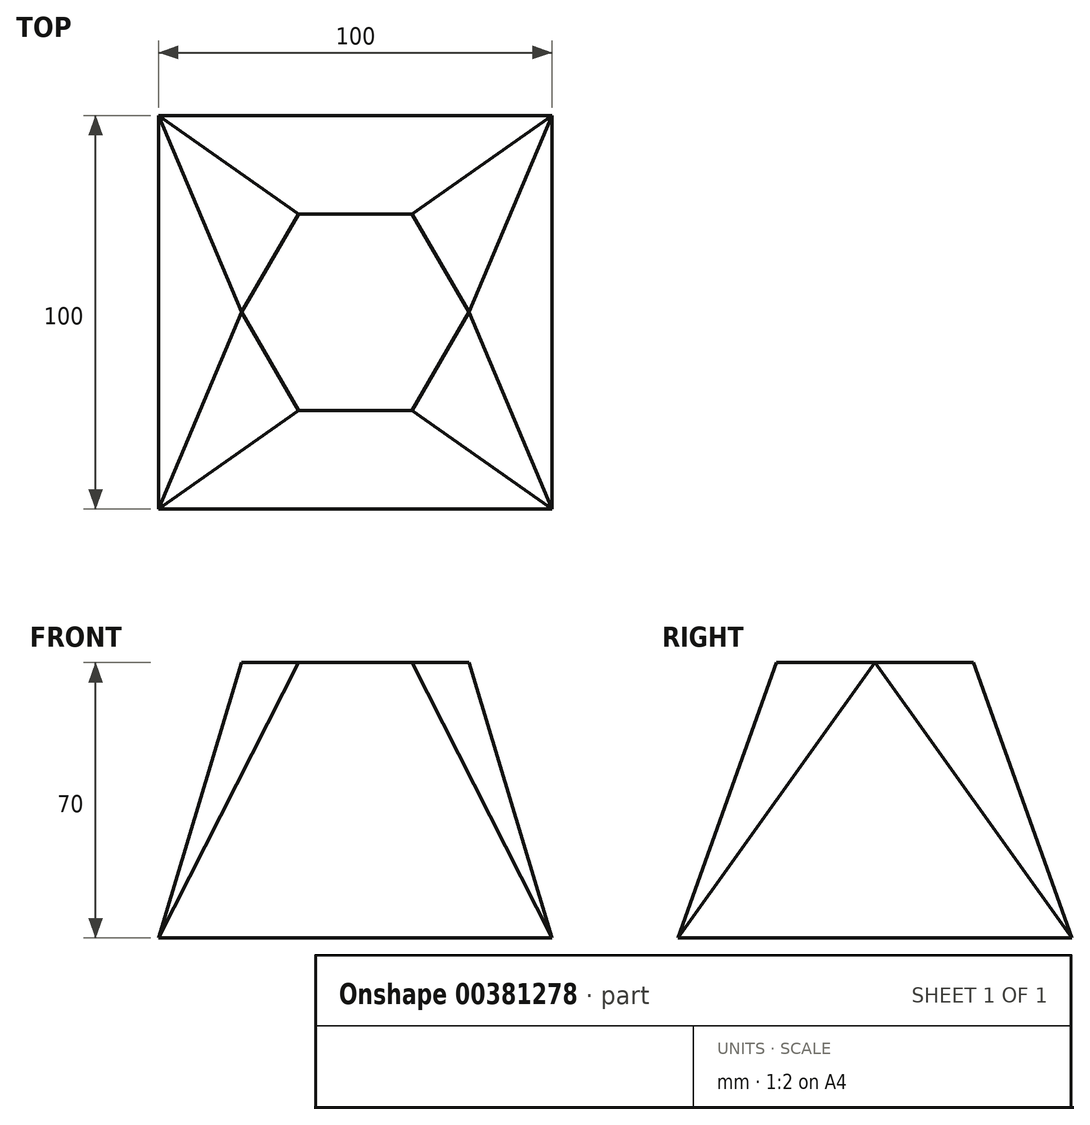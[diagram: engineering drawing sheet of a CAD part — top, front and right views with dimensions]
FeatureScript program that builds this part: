
annotation { "Feature Type Name" : "Feature", "Feature Type Description" : "" }
export const myFeature = defineFeature(function(context is Context, id is Id, definition is map)
    precondition{}
    {
        {
            var Q0;
            Q0=qCreatedBy(makeId("Top.planeOp"),FACE);
            cPlane(context, id + "F0", {"entities" : qUnion([Q0]), "cplaneType" : CPlaneType.OFFSET, "offset" : 70 * mm, "width" : 150 * mm, "height" : 150 * mm});
        }
        {
            var Q0;
            Q0=qCreatedBy(makeId("Top.planeOp"),FACE);
            var sketch = newSketch(context, id + "F1", { "sketchPlane" : qUnion([Q0])});
            skLineSegment(sketch, "E0.bottom", {"start": v(50, 50) * mm, "end": v(-50, 50) * mm});
            skLineSegment(sketch, "E0.top", {"start": v(50, -50) * mm, "end": v(-50, -50) * mm});
            skLineSegment(sketch, "E0.left", {"start": v(50, 50) * mm, "end": v(50, -50) * mm});
            skLineSegment(sketch, "E0.right", {"start": v(-50, 50) * mm, "end": v(-50, -50) * mm});
            skPoint(sketch, "E0.middle", {"position": v(0, 0) * mm});
            skSolve(sketch);
        }
        {
            var Q0;
            Q0=qCreatedBy(id+"F0.planeOp",FACE);
            var sketch = newSketch(context, id + "F2", { "sketchPlane" : qUnion([Q0])});
            skCircle(sketch, "E1.cCircle", {"center": v(0, 0) * mm, "radius": 25 * mm, "construction": true});
            skLineSegment(sketch, "E1.0", {"start": v(-14.43, 25) * mm, "end": v(14.43, 25) * mm});
            skLineSegment(sketch, "E1.1", {"start": v(14.43, 25) * mm, "end": v(28.87, 0) * mm});
            skLineSegment(sketch, "E1.2", {"start": v(28.87, 0) * mm, "end": v(14.43, -25) * mm});
            skLineSegment(sketch, "E1.3", {"start": v(14.43, -25) * mm, "end": v(-14.43, -25) * mm});
            skLineSegment(sketch, "E1.4", {"start": v(-14.43, -25) * mm, "end": v(-28.87, 0) * mm});
            skLineSegment(sketch, "E1.5", {"start": v(-28.87, 0) * mm, "end": v(-14.43, 25) * mm});
            skPoint(sketch, "E1.0.midPoint", {"position": v(0, 25) * mm});
            skSolve(sketch);
        }
        {
            var Q0;
            Q0=qCreatedBy(id+"F0.planeOp",FACE);
            var sketch = newSketch(context, id + "F3", { "sketchPlane" : qUnion([Q0])});
            skLineSegment(sketch, "E2.bottom", {"start": v(-28.87, 25) * mm, "end": v(28.87, 25) * mm});
            skLineSegment(sketch, "E2.top", {"start": v(-28.87, -25) * mm, "end": v(28.87, -25) * mm});
            skLineSegment(sketch, "E2.left", {"start": v(-28.87, 25) * mm, "end": v(-28.87, -25) * mm});
            skLineSegment(sketch, "E2.right", {"start": v(28.87, 25) * mm, "end": v(28.87, -25) * mm});
            skPoint(sketch, "E2.middle", {"position": v(0, 0) * mm});
            skSolve(sketch);
        }
        {
            var Q0;
            Q0=makeQuery(id+"F3.imprint","IMPRINT",FACE,{"disambiguationData":[TD([[makeQuery(id+"F3.imprint","IMPRINT",EDGE,{"derivedFrom":sQuery(id+"F3.wireOp",EDGE,"E2.bottom")}),-1.0]])]});
            var Q1;
            Q1=makeQuery(id+"F1.imprint","IMPRINT",FACE,{"disambiguationData":[TD([[makeQuery(id+"F1.imprint","IMPRINT",EDGE,{"derivedFrom":sQuery(id+"F1.wireOp",EDGE,"E0.bottom")}),1.0]])]});
            loft(context, id + "F4", {"sheetProfilesArray" : [{ "sheetProfileEntities" : qUnion([Q0]) }, { "sheetProfileEntities" : qUnion([Q1]) }]});
        }
        {
            var Q0;
            Q0=qCreatedBy(id+"F0.planeOp",FACE);
            var sketch = newSketch(context, id + "F5", { "sketchPlane" : qUnion([Q0])});
            skLineSegment(sketch, "E3", {"start": v(14.43, 25) * mm, "end": v(28.87, 0) * mm});
            skLineSegment(sketch, "E4", {"start": v(28.87, 0) * mm, "end": v(28.87, 25) * mm});
            skLineSegment(sketch, "E5", {"start": v(28.87, 25) * mm, "end": v(14.43, 25) * mm});
            skSolve(sketch);
        }
        {
            var Q1;
            Q1=makeQuery(id+"F5.imprint","IMPRINT",FACE,{"disambiguationData":[TD([[makeQuery(id+"F5.imprint","IMPRINT",EDGE,{"derivedFrom":sQuery(id+"F5.wireOp",EDGE,"E3")}),1.0]])]});
            var Q2;
            Q2=makeQuery(id+"F4.opLoft","MID_CAP_VERTEX",VERTEX,{"disambiguationData":[OSD([sQuery(id+"F1.wireOp",EDGE,"E0.bottom"),sQuery(id+"F1.wireOp",EDGE,"E0.left")])],"capPos":1.0});
            loft(context, id + "F6", {"sheetProfilesArray" : [{ "sheetProfileEntities" : qUnion([Q1]) }, { "sheetProfileEntities" : qUnion([Q2]) }]});
        }
        {
            var Q0;
            Q0=makeQuery(id+"F6.opLoft","SWEPT_BODY",BODY,{"disambiguationData":[OSD([sQuery(id+"F1.wireOp",EDGE,"E0.bottom"),sQuery(id+"F1.wireOp",EDGE,"E0.left"),makeQuery(id+"F5.imprint","IMPRINT",FACE,{"disambiguationData":[TD([[makeQuery(id+"F5.imprint","IMPRINT",EDGE,{"derivedFrom":sQuery(id+"F5.wireOp",EDGE,"E3")}),1.0]])]})])]});
            var Q1;
            Q1=qCreatedBy(makeId("Right.planeOp"),FACE);
            mirror(context, id + "F7", {"entities" : qUnion([Q0]), "mirrorPlane" : qUnion([Q1])});
        }
        {
            var Q0;
            Q0=makeQuery(id+"F6.opLoft","SWEPT_BODY",BODY,{"disambiguationData":[OSD([sQuery(id+"F1.wireOp",EDGE,"E0.bottom"),sQuery(id+"F1.wireOp",EDGE,"E0.left"),makeQuery(id+"F5.imprint","IMPRINT",FACE,{"disambiguationData":[TD([[makeQuery(id+"F5.imprint","IMPRINT",EDGE,{"derivedFrom":sQuery(id+"F5.wireOp",EDGE,"E3")}),1.0]])]})])]});
            var Q1;
            Q1=makeQuery(id+"F7.opPattern","COPY",BODY,{"derivedFrom":makeQuery(id+"F6.opLoft","SWEPT_BODY",BODY,{"disambiguationData":[OSD([sQuery(id+"F1.wireOp",EDGE,"E0.bottom"),sQuery(id+"F1.wireOp",EDGE,"E0.left"),makeQuery(id+"F5.imprint","IMPRINT",FACE,{"disambiguationData":[TD([[makeQuery(id+"F5.imprint","IMPRINT",EDGE,{"derivedFrom":sQuery(id+"F5.wireOp",EDGE,"E3")}),1.0]])]})])]}),"instanceName":"1"});
            var Q2;
            Q2=qCreatedBy(makeId("Front.planeOp"),FACE);
            mirror(context, id + "F8", {"entities" : qUnion([Q0, Q1]), "mirrorPlane" : qUnion([Q2])});
        }
        {
            var Q0;
            Q0=makeQuery(id+"F8.opPattern","COPY",BODY,{"derivedFrom":makeQuery(id+"F7.opPattern","COPY",BODY,{"derivedFrom":makeQuery(id+"F6.opLoft","SWEPT_BODY",BODY,{"disambiguationData":[OSD([sQuery(id+"F1.wireOp",EDGE,"E0.bottom"),sQuery(id+"F1.wireOp",EDGE,"E0.left"),makeQuery(id+"F5.imprint","IMPRINT",FACE,{"disambiguationData":[TD([[makeQuery(id+"F5.imprint","IMPRINT",EDGE,{"derivedFrom":sQuery(id+"F5.wireOp",EDGE,"E3")}),1.0]])]})])]}),"instanceName":"1"}),"instanceName":"1"});
            var Q1;
            Q1=makeQuery(id+"F8.opPattern","COPY",BODY,{"derivedFrom":makeQuery(id+"F6.opLoft","SWEPT_BODY",BODY,{"disambiguationData":[OSD([sQuery(id+"F1.wireOp",EDGE,"E0.bottom"),sQuery(id+"F1.wireOp",EDGE,"E0.left"),makeQuery(id+"F5.imprint","IMPRINT",FACE,{"disambiguationData":[TD([[makeQuery(id+"F5.imprint","IMPRINT",EDGE,{"derivedFrom":sQuery(id+"F5.wireOp",EDGE,"E3")}),1.0]])]})])]}),"instanceName":"1"});
            var Q2;
            Q2=makeQuery(id+"F7.opPattern","COPY",BODY,{"derivedFrom":makeQuery(id+"F6.opLoft","SWEPT_BODY",BODY,{"disambiguationData":[OSD([sQuery(id+"F1.wireOp",EDGE,"E0.bottom"),sQuery(id+"F1.wireOp",EDGE,"E0.left"),makeQuery(id+"F5.imprint","IMPRINT",FACE,{"disambiguationData":[TD([[makeQuery(id+"F5.imprint","IMPRINT",EDGE,{"derivedFrom":sQuery(id+"F5.wireOp",EDGE,"E3")}),1.0]])]})])]}),"instanceName":"1"});
            var Q3;
            Q3=makeQuery(id+"F6.opLoft","SWEPT_BODY",BODY,{"disambiguationData":[OSD([sQuery(id+"F1.wireOp",EDGE,"E0.bottom"),sQuery(id+"F1.wireOp",EDGE,"E0.left"),makeQuery(id+"F5.imprint","IMPRINT",FACE,{"disambiguationData":[TD([[makeQuery(id+"F5.imprint","IMPRINT",EDGE,{"derivedFrom":sQuery(id+"F5.wireOp",EDGE,"E3")}),1.0]])]})])]});
            var Q4;
            Q4=makeQuery(id+"F4.opLoft","SWEPT_BODY",BODY,{"disambiguationData":[OSD([makeQuery(id+"F1.imprint","IMPRINT",FACE,{"disambiguationData":[TD([[makeQuery(id+"F1.imprint","IMPRINT",EDGE,{"derivedFrom":sQuery(id+"F1.wireOp",EDGE,"E0.bottom")}),1.0]])]}),makeQuery(id+"F3.imprint","IMPRINT",FACE,{"disambiguationData":[TD([[makeQuery(id+"F3.imprint","IMPRINT",EDGE,{"derivedFrom":sQuery(id+"F3.wireOp",EDGE,"E2.bottom")}),-1.0]])]})])]});
            booleanBodies(context, id + "F9", {"operationType" : BooleanOperationType.SUBTRACTION, "tools" : qUnion([Q0, Q1, Q2, Q3]), "targets" : qUnion([Q4])});
        }
    });
